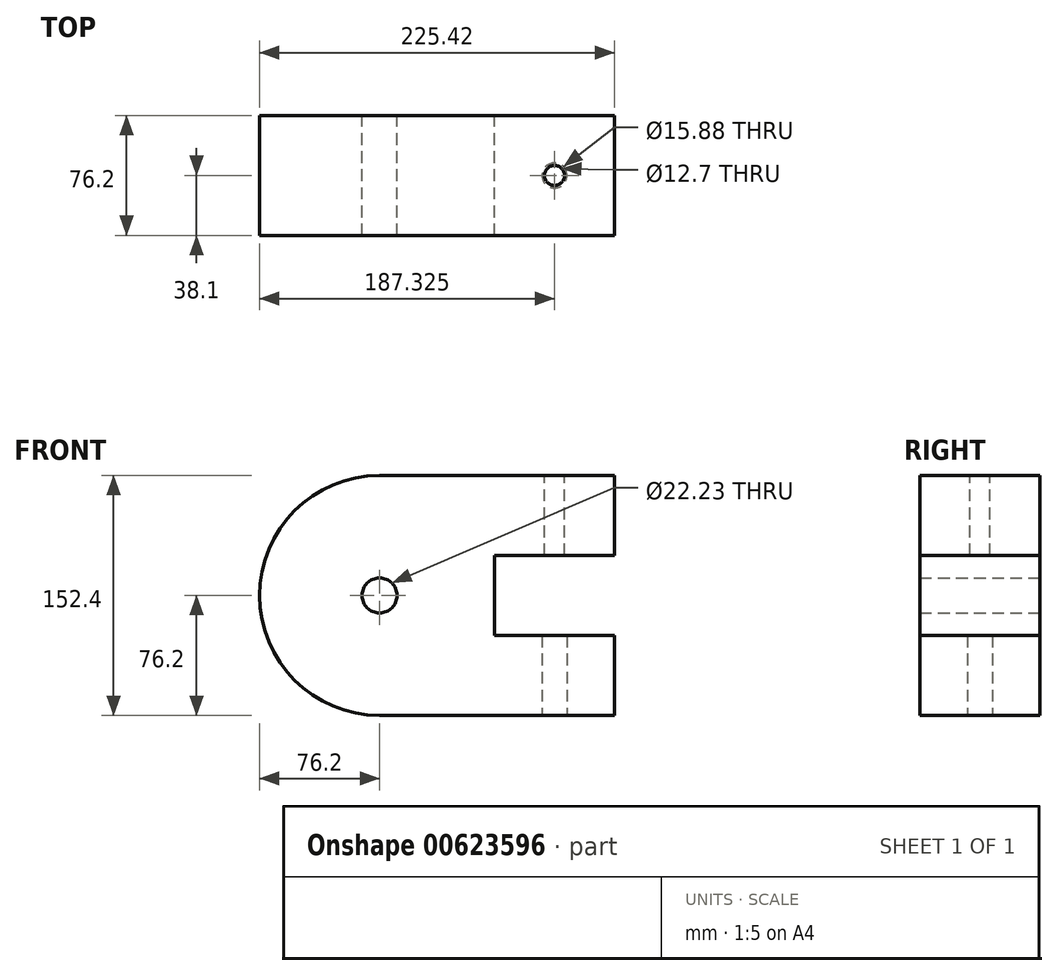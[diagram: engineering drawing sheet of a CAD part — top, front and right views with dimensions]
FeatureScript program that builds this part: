
annotation { "Feature Type Name" : "Feature", "Feature Type Description" : "" }
export const myFeature = defineFeature(function(context is Context, id is Id, definition is map)
    precondition{}
    {
        {
            var Q0;
            Q0=qCreatedBy(makeId("Front.planeOp"),FACE);
            var sketch = newSketch(context, id + "F0", { "sketchPlane" : qUnion([Q0])});
            skLineSegment(sketch, "E0", {"start": v(0, 0) * mm, "end": v(149.23, 0) * mm});
            skLineSegment(sketch, "E1", {"start": v(149.23, 0) * mm, "end": v(149.23, 50.8) * mm});
            skLineSegment(sketch, "E2", {"start": v(149.23, 50.8) * mm, "end": v(73.03, 50.8) * mm});
            skLineSegment(sketch, "E3", {"start": v(73.03, 50.8) * mm, "end": v(73.03, 101.6) * mm});
            skLineSegment(sketch, "E4", {"start": v(73.03, 101.6) * mm, "end": v(149.23, 101.6) * mm});
            skLineSegment(sketch, "E5", {"start": v(149.23, 101.6) * mm, "end": v(149.23, 152.4) * mm});
            skLineSegment(sketch, "E6", {"start": v(149.23, 152.4) * mm, "end": v(0, 152.4) * mm});
            skArc(sketch, "E7", {"start": v(0, 152.4) * mm, "mid": v(-76.2, 76.2) * mm, "end": v(0, 0) * mm});
            skCircle(sketch, "E8", {"center": v(0, 76.2) * mm, "radius": 11.11 * mm});
            skSolve(sketch);
        }
        {
            var Q0;
            Q0=makeQuery(id+"F0.imprint","IMPRINT",FACE,{"disambiguationData":[TD([[makeQuery(id+"F0.imprint","IMPRINT",EDGE,{"derivedFrom":sQuery(id+"F0.wireOp",EDGE,"E0")}),1.0]])]});
            extrude(context, id + "F1", {"entities" : qUnion([Q0]), "depth" : 76.2 * mm, "offsetDistance" : 25.4 * mm});
        }
        {
            var Q0;
            Q0=makeQuery(id+"F1.opExtrude","SWEPT_FACE",FACE,{"disambiguationData":[OSD([sQuery(id+"F0.wireOp",EDGE,"E6")])]});
            var sketch = newSketch(context, id + "F2", { "sketchPlane" : qUnion([Q0])});
            skCircle(sketch, "E9", {"center": v(111.13, -38.1) * mm, "radius": 6.35 * mm});
            skSolve(sketch);
        }
        {
            var Q0;
            Q0=makeQuery(id+"F1.opExtrude","SWEPT_FACE",FACE,{"disambiguationData":[OSD([sQuery(id+"F0.wireOp",EDGE,"E0")])]});
            var sketch = newSketch(context, id + "F3", { "sketchPlane" : qUnion([Q0])});
            skCircle(sketch, "E10", {"center": v(111.13, 38.1) * mm, "radius": 7.94 * mm});
            skSolve(sketch);
        }
        {
            var Q0;
            Q0 = qSketchRegion(id + "F3", true);
            extrude(context, id + "F4", {"entities" : qUnion([Q0]), "operationType" : NewBodyOperationType.REMOVE, "oppositeDirection" : true, "depth" : 50.8 * mm, "offsetDistance" : 25.4 * mm});
        }
        {
            var Q0;
            Q0=makeQuery(id+"F2.imprint","IMPRINT",FACE,{"disambiguationData":[TD([[makeQuery(id+"F2.imprint","IMPRINT",EDGE,{"derivedFrom":sQuery(id+"F2.wireOp",EDGE,"E9")}),1.0]])]});
            extrude(context, id + "F5", {"entities" : qUnion([Q0]), "operationType" : NewBodyOperationType.REMOVE, "oppositeDirection" : true, "depth" : 50.8 * mm, "offsetDistance" : 25.4 * mm});
        }
    });
